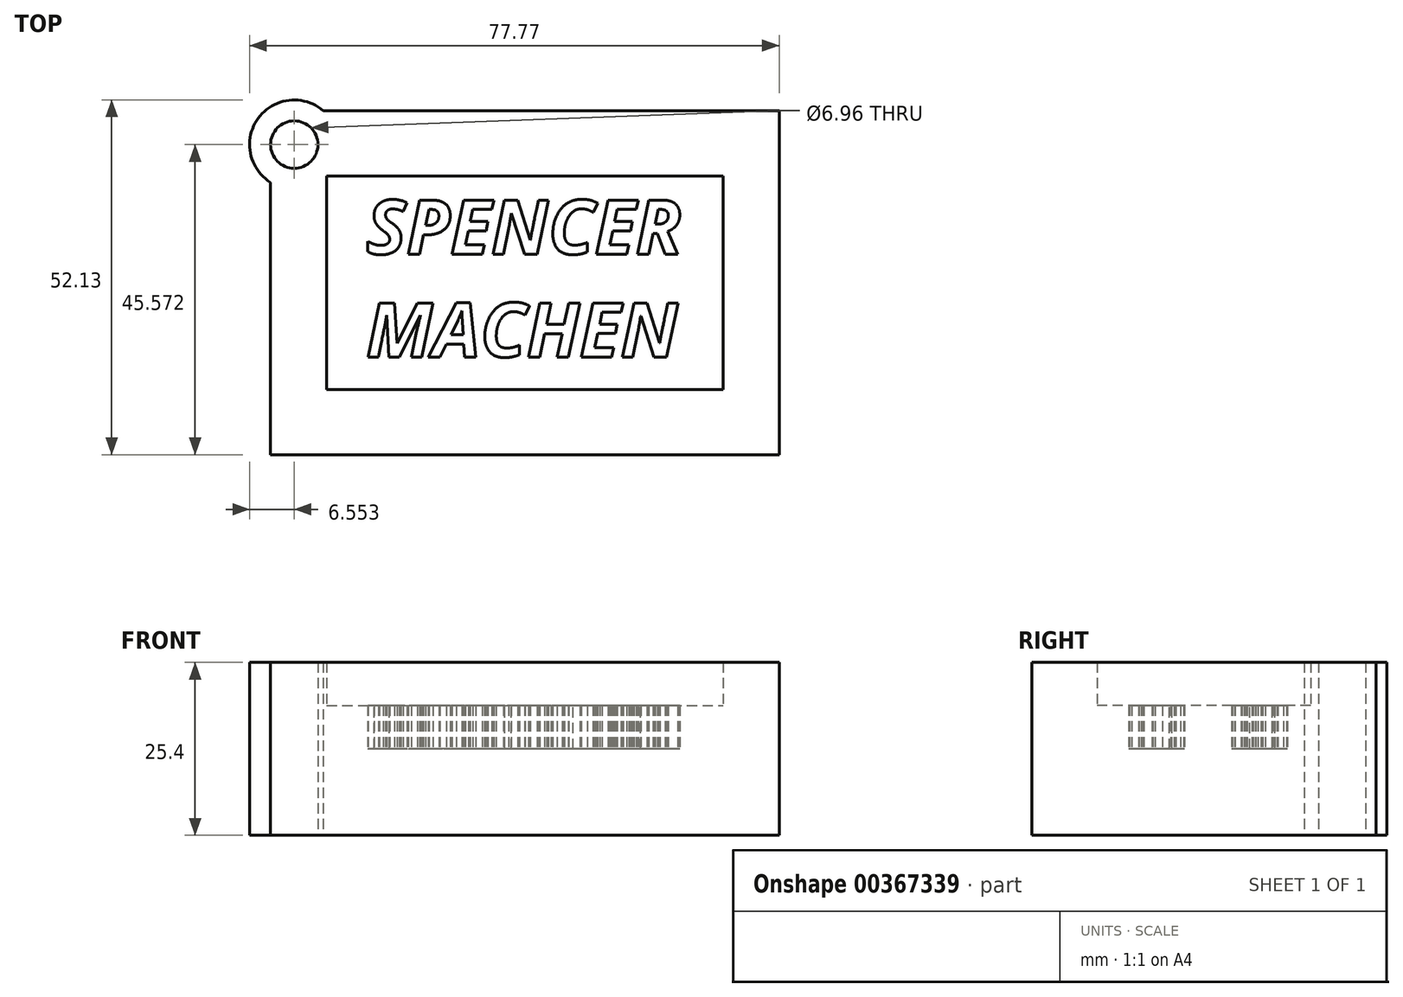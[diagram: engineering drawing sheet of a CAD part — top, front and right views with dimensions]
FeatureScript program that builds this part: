
annotation { "Feature Type Name" : "Feature", "Feature Type Description" : "" }
export const myFeature = defineFeature(function(context is Context, id is Id, definition is map)
    precondition{}
    {
        {
            var Q0;
            Q0=qCreatedBy(makeId("Top.planeOp"),FACE);
            var sketch = newSketch(context, id + "F0", { "sketchPlane" : qUnion([Q0])});
            skText(sketch, "E0", { "text": "SPENCER\nMACHEN", "fontName": "OpenSans-BoldItalic.ttf"});
            skLineSegment(sketch, "E1.bottom", {"start": v(29.1, -15.67) * mm, "end": v(-29.1, -15.67) * mm});
            skLineSegment(sketch, "E1.top", {"start": v(29.1, 15.67) * mm, "end": v(-29.1, 15.67) * mm});
            skLineSegment(sketch, "E1.left", {"start": v(29.1, -15.67) * mm, "end": v(29.1, 15.67) * mm});
            skLineSegment(sketch, "E1.right", {"start": v(-29.1, -15.67) * mm, "end": v(-29.1, 15.67) * mm});
            skPoint(sketch, "E1.middle", {"position": v(0, 0) * mm});
            skLineSegment(sketch, "E2.bottom", {"start": v(37.35, -25.28) * mm, "end": v(-37.35, -25.28) * mm});
            skLineSegment(sketch, "E2.top", {"start": v(37.35, 25.28) * mm, "end": v(-37.35, 25.28) * mm});
            skLineSegment(sketch, "E2.left", {"start": v(37.35, -25.28) * mm, "end": v(37.35, 25.28) * mm});
            skLineSegment(sketch, "E2.right", {"start": v(-37.35, -25.28) * mm, "end": v(-37.35, 25.28) * mm});
            skCircle(sketch, "E3", {"center": v(-33.87, 20.3) * mm, "radius": 3.48 * mm});
            skCircle(sketch, "E4", {"center": v(-33.87, 20.3) * mm, "radius": 6.55 * mm});
            const initialGuessF0  = {"E0": [-0.0233, 0.0042, 1, 0, 0.008]};
            skSetInitialGuess(sketch, initialGuessF0);
            skSolve(sketch);
        }
        {
            var Q0;
            Q0=makeQuery(id+"F0.imprint","IMPRINT",FACE,{"disambiguationData":[TD([[makeQuery(id+"F0.imprint","IMPRINT",EDGE,{"derivedFrom":sQuery(id+"F0.wireOp",EDGE,"E1.bottom")}),1.0]])]});
            var Q1;
            Q1=makeQuery(id+"F0.imprint","IMPRINT",FACE,{"disambiguationData":[TD([[makeQuery(id+"F0.imprint","IMPRINT",EDGE,{"derivedFrom":sQuery(id+"F0.wireOp",EDGE,"E0.sketch_text.stroke-60")}),1.0]])]});
            var Q2;
            Q2=makeQuery(id+"F0.imprint","IMPRINT",FACE,{"disambiguationData":[TD([[makeQuery(id+"F0.imprint","IMPRINT",EDGE,{"derivedFrom":sQuery(id+"F0.wireOp",EDGE,"E0.sketch_text.stroke-0")}),1.0]])]});
            var Q3;
            Q3=makeQuery(id+"F0.imprint","IMPRINT",FACE,{"disambiguationData":[TD([[makeQuery(id+"F0.imprint","IMPRINT",EDGE,{"derivedFrom":sQuery(id+"F0.wireOp",EDGE,"E0.sketch_text.stroke-52")}),-1.0]])]});
            var Q4;
            Q4=makeQuery(id+"F0.imprint","IMPRINT",FACE,{"disambiguationData":[TD([[makeQuery(id+"F0.imprint","IMPRINT",EDGE,{"derivedFrom":sQuery(id+"F0.wireOp",EDGE,"E0.sketch_text.stroke-78")}),-1.0]])]});
            var Q5;
            Q5=makeQuery(id+"F0.imprint","IMPRINT",FACE,{"disambiguationData":[TD([[makeQuery(id+"F0.imprint","IMPRINT",EDGE,{"derivedFrom":sQuery(id+"F0.wireOp",EDGE,"E0.sketch_text.stroke-18")}),-1.0]])]});
            var Q6;
            Q6=makeQuery(id+"F0.imprint","IMPRINT",FACE,{"disambiguationData":[TD([[makeQuery(id+"F0.imprint","IMPRINT",EDGE,{"derivedFrom":sQuery(id+"F0.wireOp",EDGE,"E0.sketch_text.stroke-0")}),-1.0]])]});
            var Q7;
            Q7=makeQuery(id+"F0.imprint","IMPRINT",FACE,{"disambiguationData":[TD([[makeQuery(id+"F0.imprint","IMPRINT",EDGE,{"derivedFrom":sQuery(id+"F0.wireOp",EDGE,"E0.sketch_text.stroke-66")}),-1.0]])]});
            var Q8;
            Q8=makeQuery(id+"F0.imprint","IMPRINT",FACE,{"disambiguationData":[TD([[makeQuery(id+"F0.imprint","IMPRINT",EDGE,{"derivedFrom":sQuery(id+"F0.wireOp",EDGE,"E0.sketch_text.stroke-22")}),-1.0]])]});
            var Q9;
            Q9=makeQuery(id+"F0.imprint","IMPRINT",FACE,{"disambiguationData":[TD([[makeQuery(id+"F0.imprint","IMPRINT",EDGE,{"derivedFrom":sQuery(id+"F0.wireOp",EDGE,"E0.sketch_text.stroke-40")}),-1.0]])]});
            extrude(context, id + "F1", {"entities" : qUnion([Q0, Q1, Q2, Q3, Q4, Q5, Q6, Q7, Q8, Q9]), "depth" : 6.35 * mm});
        }
        {
            var Q0;
            Q0 = qSketchRegion(id + "F0", true);
            extrude(context, id + "F2", {"entities" : qUnion([Q0]), "operationType" : NewBodyOperationType.ADD, "depth" : 25.4 * mm});
        }
        {
            var Q0;
            Q0=makeQuery(id+"F0.imprint","IMPRINT",FACE,{"disambiguationData":[TD([[makeQuery(id+"F0.imprint","IMPRINT",EDGE,{"derivedFrom":sQuery(id+"F0.wireOp",EDGE,"E0.sketch_text.stroke-0")}),-1.0]])]});
            var Q1;
            Q1=makeQuery(id+"F0.imprint","IMPRINT",FACE,{"disambiguationData":[TD([[makeQuery(id+"F0.imprint","IMPRINT",EDGE,{"derivedFrom":sQuery(id+"F0.wireOp",EDGE,"E0.sketch_text.stroke-18")}),-1.0]])]});
            var Q2;
            Q2=makeQuery(id+"F0.imprint","IMPRINT",FACE,{"disambiguationData":[TD([[makeQuery(id+"F0.imprint","IMPRINT",EDGE,{"derivedFrom":sQuery(id+"F0.wireOp",EDGE,"E0.sketch_text.stroke-22")}),-1.0]])]});
            var Q3;
            Q3=makeQuery(id+"F0.imprint","IMPRINT",FACE,{"disambiguationData":[TD([[makeQuery(id+"F0.imprint","IMPRINT",EDGE,{"derivedFrom":sQuery(id+"F0.wireOp",EDGE,"E0.sketch_text.stroke-40")}),-1.0]])]});
            var Q4;
            Q4=makeQuery(id+"F0.imprint","IMPRINT",FACE,{"disambiguationData":[TD([[makeQuery(id+"F0.imprint","IMPRINT",EDGE,{"derivedFrom":sQuery(id+"F0.wireOp",EDGE,"E0.sketch_text.stroke-52")}),-1.0]])]});
            var Q5;
            Q5=makeQuery(id+"F0.imprint","IMPRINT",FACE,{"disambiguationData":[TD([[makeQuery(id+"F0.imprint","IMPRINT",EDGE,{"derivedFrom":sQuery(id+"F0.wireOp",EDGE,"E0.sketch_text.stroke-66")}),-1.0]])]});
            var Q6;
            Q6=makeQuery(id+"F0.imprint","IMPRINT",FACE,{"disambiguationData":[TD([[makeQuery(id+"F0.imprint","IMPRINT",EDGE,{"derivedFrom":sQuery(id+"F0.wireOp",EDGE,"E0.sketch_text.stroke-78")}),-1.0]])]});
            extrude(context, id + "F3", {"entities" : qUnion([Q0, Q1, Q2, Q3, Q4, Q5, Q6]), "operationType" : NewBodyOperationType.ADD, "depth" : 12.7 * mm});
        }
        {
            var Q0;
            Q0=makeQuery(id+"F3.boolean.opBoolean","SPLIT",FACE,{"disambiguationData":[TD([makeQuery(id+"F2.opExtrude","SWEPT_FACE",FACE,{"disambiguationData":[OSD([sQuery(id+"F0.wireOp",EDGE,"E1.bottom")])]})])],"derivedFrom":makeQuery(id+"F1.opExtrude","CAP_FACE",FACE,{"disambiguationData":[OSD([sQuery(id+"F0.wireOp",EDGE,"E2.bottom"),sQuery(id+"F0.wireOp",EDGE,"E2.top"),sQuery(id+"F0.wireOp",EDGE,"E2.left"),sQuery(id+"F0.wireOp",EDGE,"E2.right")])],"isStart":false})});
            extrude(context, id + "F4", {"entities" : qUnion([Q0]), "operationType" : NewBodyOperationType.ADD, "depth" : 12.7 * mm});
        }
        {
            var Q0;
            Q0=makeQuery(id+"F0.imprint","IMPRINT",FACE,{"disambiguationData":[TD([[makeQuery(id+"F0.imprint","IMPRINT",EDGE,{"derivedFrom":sQuery(id+"F0.wireOp",EDGE,"E0.sketch_text.stroke-115")}),-1.0]])]});
            var Q1;
            Q1=makeQuery(id+"F0.imprint","IMPRINT",FACE,{"disambiguationData":[TD([[makeQuery(id+"F0.imprint","IMPRINT",EDGE,{"derivedFrom":sQuery(id+"F0.wireOp",EDGE,"E0.sketch_text.stroke-133")}),-1.0]])]});
            var Q2;
            Q2=makeQuery(id+"F0.imprint","IMPRINT",FACE,{"disambiguationData":[TD([[makeQuery(id+"F0.imprint","IMPRINT",EDGE,{"derivedFrom":sQuery(id+"F0.wireOp",EDGE,"E0.sketch_text.stroke-24")}),-1.0]])]});
            var Q3;
            Q3=makeQuery(id+"F0.imprint","IMPRINT",FACE,{"disambiguationData":[TD([[makeQuery(id+"F0.imprint","IMPRINT",EDGE,{"derivedFrom":sQuery(id+"F0.wireOp",EDGE,"E0.sketch_text.stroke-84")}),-1.0]])]});
            var Q4;
            Q4=makeQuery(id+"F0.imprint","IMPRINT",FACE,{"disambiguationData":[TD([[makeQuery(id+"F0.imprint","IMPRINT",EDGE,{"derivedFrom":sQuery(id+"F0.wireOp",EDGE,"E0.sketch_text.stroke-96")}),-1.0]])]});
            var Q5;
            Q5=makeQuery(id+"F0.imprint","IMPRINT",FACE,{"disambiguationData":[TD([[makeQuery(id+"F0.imprint","IMPRINT",EDGE,{"derivedFrom":sQuery(id+"F0.wireOp",EDGE,"E0.sketch_text.stroke-189")}),-1.0]])]});
            var Q6;
            Q6=makeQuery(id+"F0.imprint","IMPRINT",FACE,{"disambiguationData":[TD([[makeQuery(id+"F0.imprint","IMPRINT",EDGE,{"derivedFrom":sQuery(id+"F0.wireOp",EDGE,"E0.sketch_text.stroke-177")}),-1.0]])]});
            var Q7;
            Q7=makeQuery(id+"F0.imprint","IMPRINT",FACE,{"disambiguationData":[TD([[makeQuery(id+"F0.imprint","IMPRINT",EDGE,{"derivedFrom":sQuery(id+"F0.wireOp",EDGE,"E0.sketch_text.stroke-165")}),-1.0]])]});
            var Q8;
            Q8=makeQuery(id+"F0.imprint","IMPRINT",FACE,{"disambiguationData":[TD([[makeQuery(id+"F0.imprint","IMPRINT",EDGE,{"derivedFrom":sQuery(id+"F0.wireOp",EDGE,"E0.sketch_text.stroke-147")}),-1.0]])]});
            extrude(context, id + "F5", {"entities" : qUnion([Q0, Q1, Q2, Q3, Q4, Q5, Q6, Q7, Q8]), "operationType" : NewBodyOperationType.ADD, "depth" : 12.7 * mm});
        }
        {
            var Q0;
            Q0=makeQuery(id+"F0.imprint","IMPRINT",FACE,{"disambiguationData":[TD([[makeQuery(id+"F0.imprint","IMPRINT",EDGE,{"derivedFrom":sQuery(id+"F0.wireOp",EDGE,"E0.sketch_text.stroke-24")}),1.0]])]});
            var Q1;
            Q1=makeQuery(id+"F0.imprint","IMPRINT",FACE,{"disambiguationData":[TD([[makeQuery(id+"F0.imprint","IMPRINT",EDGE,{"derivedFrom":sQuery(id+"F0.wireOp",EDGE,"E0.sketch_text.stroke-96")}),1.0]])]});
            var Q2;
            Q2=makeQuery(id+"F0.imprint","IMPRINT",FACE,{"disambiguationData":[TD([[makeQuery(id+"F0.imprint","IMPRINT",EDGE,{"derivedFrom":sQuery(id+"F0.wireOp",EDGE,"E0.sketch_text.stroke-141")}),1.0]])]});
            extrude(context, id + "F6", {"entities" : qUnion([Q0, Q1, Q2]), "operationType" : NewBodyOperationType.ADD, "depth" : 19.05 * mm});
        }
    });
